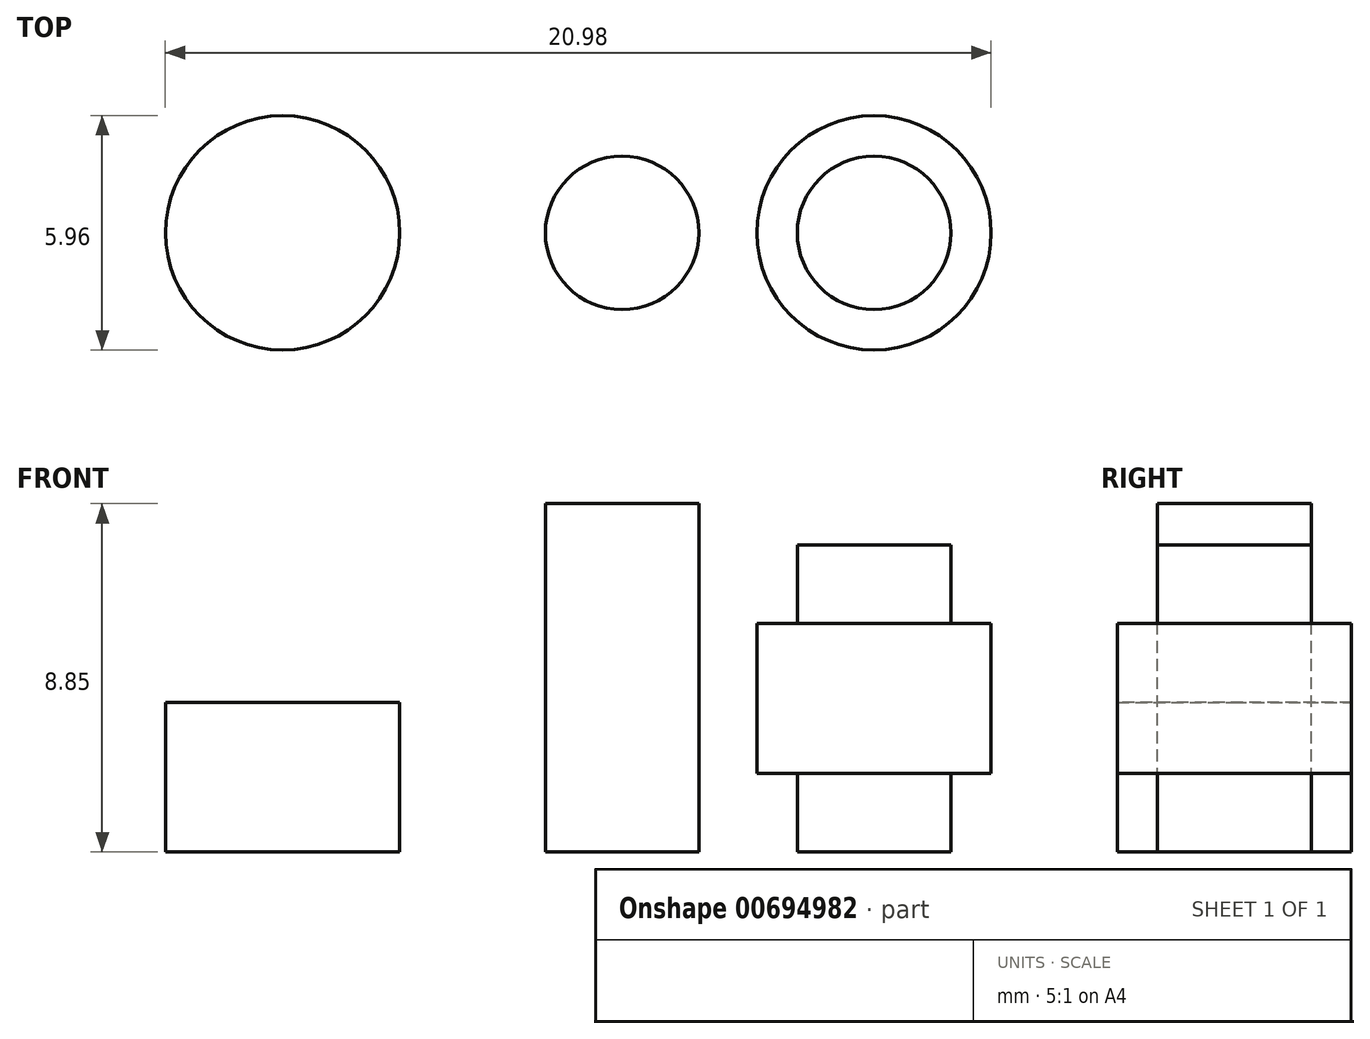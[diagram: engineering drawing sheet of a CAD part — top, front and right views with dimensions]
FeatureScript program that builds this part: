
annotation { "Feature Type Name" : "Feature", "Feature Type Description" : "" }
export const myFeature = defineFeature(function(context is Context, id is Id, definition is map)
    precondition{}
    {
        {
            var Q0;
            Q0=qCreatedBy(makeId("Front.planeOp"),FACE);
            var sketch = newSketch(context, id + "F0", { "sketchPlane" : qUnion([Q0])});
            skLineSegment(sketch, "E0", {"start": v(0, 0) * mm, "end": v(2.97, 0) * mm});
            skLineSegment(sketch, "E1", {"start": v(2.97, 0) * mm, "end": v(2.97, 3.8) * mm});
            skLineSegment(sketch, "E2", {"start": v(2.97, 3.8) * mm, "end": v(0, 3.8) * mm});
            skLineSegment(sketch, "E3", {"start": v(0, 3.8) * mm, "end": v(0, 0) * mm});
            skSolve(sketch);
        }
        {
            var Q0;
            Q0 = qSketchRegion(id + "F0", true);
            var Q1;
            Q1=sQuery(id+"F0.wireOp",EDGE,"E3");
            revolve(context, id + "F1", {"entities" : qUnion([Q0]), "axis" : qUnion([Q1]), "revolveType" : RevolveType.FULL});
        }
        {
            var Q0;
            Q0=qCreatedBy(makeId("Front.planeOp"),FACE);
            var sketch = newSketch(context, id + "F2", { "sketchPlane" : qUnion([Q0])});
            skLineSegment(sketch, "E4", {"start": v(8.62, 0) * mm, "end": v(10.57, 0) * mm});
            skLineSegment(sketch, "E5", {"start": v(10.57, 0) * mm, "end": v(10.57, 8.85) * mm});
            skLineSegment(sketch, "E6", {"start": v(10.57, 8.85) * mm, "end": v(8.62, 8.85) * mm});
            skLineSegment(sketch, "E7", {"start": v(8.62, 8.85) * mm, "end": v(8.62, 0) * mm});
            skSolve(sketch);
        }
        {
            var Q0;
            Q0 = qSketchRegion(id + "F2", true);
            var Q1;
            Q1=sQuery(id+"F2.wireOp",EDGE,"E7");
            revolve(context, id + "F3", {"entities" : qUnion([Q0]), "axis" : qUnion([Q1]), "revolveType" : RevolveType.FULL});
        }
        {
            var Q0;
            Q0=qCreatedBy(makeId("Front.planeOp"),FACE);
            var sketch = newSketch(context, id + "F4", { "sketchPlane" : qUnion([Q0])});
            skLineSegment(sketch, "E8", {"start": v(15.03, 0) * mm, "end": v(16.98, 0) * mm});
            skLineSegment(sketch, "E9", {"start": v(16.98, 0) * mm, "end": v(16.98, 2) * mm});
            skLineSegment(sketch, "E10", {"start": v(16.98, 2) * mm, "end": v(18, 2) * mm});
            skLineSegment(sketch, "E11", {"start": v(18, 2) * mm, "end": v(18, 5.8) * mm});
            skLineSegment(sketch, "E12", {"start": v(18, 5.8) * mm, "end": v(16.98, 5.8) * mm});
            skLineSegment(sketch, "E13", {"start": v(16.98, 5.8) * mm, "end": v(16.98, 7.8) * mm});
            skLineSegment(sketch, "E14", {"start": v(16.98, 7.8) * mm, "end": v(15.03, 7.8) * mm});
            skLineSegment(sketch, "E15", {"start": v(15.03, 7.8) * mm, "end": v(15.03, 0) * mm});
            skSolve(sketch);
        }
        {
            var Q0;
            Q0 = qSketchRegion(id + "F4", true);
            var Q1;
            Q1=sQuery(id+"F4.wireOp",EDGE,"E15");
            revolve(context, id + "F5", {"entities" : qUnion([Q0]), "axis" : qUnion([Q1]), "revolveType" : RevolveType.FULL});
        }
    });
